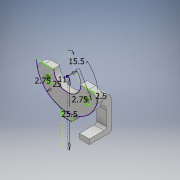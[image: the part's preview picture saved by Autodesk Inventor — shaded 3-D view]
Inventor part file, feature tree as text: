
AUTODESK INVENTOR PART (.ipt)
format: ipt  version: 2018 (Build 220112000, 112)  size: 200,704 bytes
history: native  units: mm
features: fillet x5, extrude x4, sketch x3
ambient origin geometry x8: Origin, YZ Plane, XZ Plane, XY Plane, X Axis, Y Axis, Z Axis, Center Point
bodies: Solid1 (feature_tree)
feature tree (12):
  sketch  "Sketch1"  dims[d0=11.0mm d1=25.0mm d2=15.5mm]
  extrude  "Extrusion1"  Depth=11.0mm
  fillet  "Fillet1"  Radius=15.5mm
  extrude  "Extrusion2"  Depth=2.75mm
  fillet  "Fillet2"  Radius=25.5mm
  fillet  "Fillet3"  Radius=2.5mm
  extrude  "Extrusion3"  Depth=2.0mm
  extrude  "Extrusion4"  Depth=1.0mm TaperAngle=0.0deg
  fillet  "Fillet4"  Radius=3.0mm
  fillet  "Fillet5"  Radius=14.0mm
  sketch  "Sketch2"  dims[d3=2.75mm d4=2.75mm d5=25.5mm d6=2.5mm]
  sketch  "Sketch4"  dims[d7=2.0mm d8=2.0mm d9=2.5mm d10=0.0mm d11=3.0mm d12=14.0mm d13=0.0mm d14=7.0mm d15=3.0mm d16=4.0mm d17=14.15mm d18=2.0mm d19=0.0mm d20=4.0mm d21=2.0mm d22=7.0mm d23=0.0mm d24=3.0mm d25=1.0mm]
